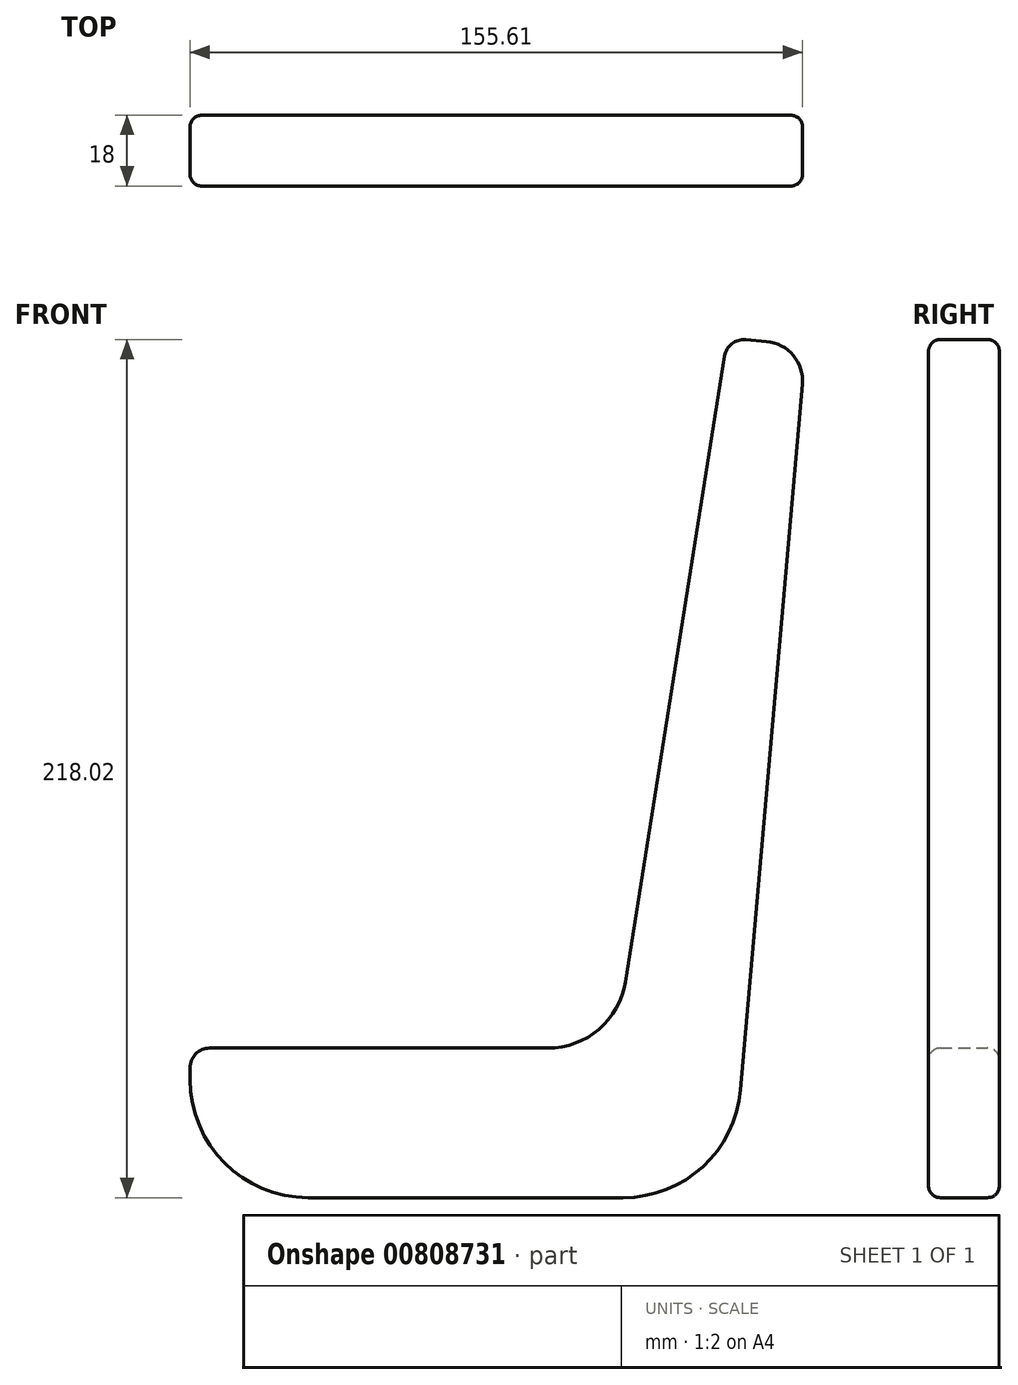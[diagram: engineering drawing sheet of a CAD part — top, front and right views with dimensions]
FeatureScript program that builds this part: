
annotation { "Feature Type Name" : "Feature", "Feature Type Description" : "" }
export const myFeature = defineFeature(function(context is Context, id is Id, definition is map)
    precondition{}
    {
        {
            var Q0;
            Q0=qCreatedBy(makeId("Front.planeOp"),FACE);
            var sketch = newSketch(context, id + "F0", { "sketchPlane" : qUnion([Q0])});
            skLineSegment(sketch, "E0", {"start": v(-17.08, 0) * mm, "end": v(-102.95, 0) * mm});
            skLineSegment(sketch, "E1", {"start": v(-107.95, -5) * mm, "end": v(-107.95, -8) * mm});
            skLineSegment(sketch, "E2", {"start": v(-77.95, -38) * mm, "end": v(2.05, -38) * mm});
            skLineSegment(sketch, "E3", {"start": v(31.94, -10.61) * mm, "end": v(47.63, 168.7) * mm});
            skLineSegment(sketch, "E4", {"start": v(38.54, 179.53) * mm, "end": v(33.22, 180) * mm});
            skLineSegment(sketch, "E5", {"start": v(27.84, 175.8) * mm, "end": v(2.67, 16.87) * mm});
            skPoint(sketch, "E6.visualSharp", {"position": v(29.54, -38) * mm});
            skArc(sketch, "E6.filletArc", {"start": v(2.05, -38) * mm, "mid": v(22.32, -30.12) * mm, "end": v(31.94, -10.61) * mm});
            skPoint(sketch, "E7.visualSharp", {"position": v(0, 0) * mm});
            skArc(sketch, "E7.filletArc", {"start": v(-17.08, 0) * mm, "mid": v(-4.1, 4.8) * mm, "end": v(2.67, 16.87) * mm});
            skPoint(sketch, "E8.visualSharp", {"position": v(-107.95, -38) * mm});
            skArc(sketch, "E8.filletArc", {"start": v(-107.95, -8) * mm, "mid": v(-99.16, -29.21) * mm, "end": v(-77.95, -38) * mm});
            skPoint(sketch, "E9.visualSharp", {"position": v(48.5, 178.66) * mm});
            skArc(sketch, "E9.filletArc", {"start": v(47.63, 168.7) * mm, "mid": v(45.32, 176) * mm, "end": v(38.54, 179.53) * mm});
            skPoint(sketch, "E10.visualSharp", {"position": v(-107.95, 0) * mm});
            skArc(sketch, "E10.filletArc", {"start": v(-102.95, 0) * mm, "mid": v(-106.48, -1.46) * mm, "end": v(-107.95, -5) * mm});
            skPoint(sketch, "E11.visualSharp", {"position": v(28.57, 180.4) * mm});
            skArc(sketch, "E11.filletArc", {"start": v(33.22, 180) * mm, "mid": v(29.7, 178.96) * mm, "end": v(27.84, 175.8) * mm});
            skLineSegment(sketch, "E12", {"start": v(-107.95, 0) * mm, "end": v(-107.95, -10) * mm, "construction": true});
            skLineSegment(sketch, "E13", {"start": v(-107.95, -10) * mm, "end": v(-57.95, -10) * mm, "construction": true});
            skPoint(sketch, "E14", {"position": v(-57.95, -10) * mm});
            skLineSegment(sketch, "E15", {"start": v(38.54, 179.53) * mm, "end": v(30.71, 130.15) * mm, "construction": true});
            skPoint(sketch, "E16", {"position": v(30.71, 130.15) * mm});
            skSolve(sketch);
        }
        {
            var Q0;
            Q0=makeQuery(id+"F0.imprint","IMPRINT",FACE,{"disambiguationData":[TD([[makeQuery(id+"F0.imprint","IMPRINT",EDGE,{"derivedFrom":sQuery(id+"F0.wireOp",EDGE,"E0")}),1.0]])]});
            extrude(context, id + "F1", {"entities" : qUnion([Q0]), "depth" : 18 * mm, "offsetDistance" : 25 * mm});
        }
        {
            var Q0;
            Q0=makeQuery(id+"F1.opExtrude","CAP_FACE",FACE,{"disambiguationData":[OSD([sQuery(id+"F0.wireOp",EDGE,"E0"),sQuery(id+"F0.wireOp",EDGE,"E1"),sQuery(id+"F0.wireOp",EDGE,"E2"),sQuery(id+"F0.wireOp",EDGE,"E3"),sQuery(id+"F0.wireOp",EDGE,"E4"),sQuery(id+"F0.wireOp",EDGE,"E5"),sQuery(id+"F0.wireOp",EDGE,"E6.filletArc"),sQuery(id+"F0.wireOp",EDGE,"E7.filletArc"),sQuery(id+"F0.wireOp",EDGE,"E8.filletArc"),sQuery(id+"F0.wireOp",EDGE,"E9.filletArc"),sQuery(id+"F0.wireOp",EDGE,"E10.filletArc"),sQuery(id+"F0.wireOp",EDGE,"E11.filletArc")])],"isStart":false});
            var sketch = newSketch(context, id + "F2", { "sketchPlane" : qUnion([Q0])});
            skPoint(sketch, "E17.0", {"position": v(30.71, 130.15) * mm});
            skPoint(sketch, "E18.0", {"position": v(-57.95, -10) * mm});
            skSolve(sketch);
        }
        {
            var Q0;
            Q0=makeQuery(id+"F1.opExtrude","CAP_FACE",FACE,{"disambiguationData":[OSD([sQuery(id+"F0.wireOp",EDGE,"E0"),sQuery(id+"F0.wireOp",EDGE,"E1"),sQuery(id+"F0.wireOp",EDGE,"E2"),sQuery(id+"F0.wireOp",EDGE,"E3"),sQuery(id+"F0.wireOp",EDGE,"E4"),sQuery(id+"F0.wireOp",EDGE,"E5"),sQuery(id+"F0.wireOp",EDGE,"E6.filletArc"),sQuery(id+"F0.wireOp",EDGE,"E7.filletArc"),sQuery(id+"F0.wireOp",EDGE,"E8.filletArc"),sQuery(id+"F0.wireOp",EDGE,"E9.filletArc"),sQuery(id+"F0.wireOp",EDGE,"E10.filletArc"),sQuery(id+"F0.wireOp",EDGE,"E11.filletArc")])],"isStart":true});
            var Q1;
            Q1=makeQuery(id+"F1.opExtrude","CAP_FACE",FACE,{"disambiguationData":[OSD([sQuery(id+"F0.wireOp",EDGE,"E0"),sQuery(id+"F0.wireOp",EDGE,"E1"),sQuery(id+"F0.wireOp",EDGE,"E2"),sQuery(id+"F0.wireOp",EDGE,"E3"),sQuery(id+"F0.wireOp",EDGE,"E4"),sQuery(id+"F0.wireOp",EDGE,"E5"),sQuery(id+"F0.wireOp",EDGE,"E6.filletArc"),sQuery(id+"F0.wireOp",EDGE,"E7.filletArc"),sQuery(id+"F0.wireOp",EDGE,"E8.filletArc"),sQuery(id+"F0.wireOp",EDGE,"E9.filletArc"),sQuery(id+"F0.wireOp",EDGE,"E10.filletArc"),sQuery(id+"F0.wireOp",EDGE,"E11.filletArc")])],"isStart":false});
            fillet(context, id + "F3", {"entities" : qUnion([Q0, Q1]), "radius" : 3 * mm, "tangentPropagation" : true, "allowEdgeOverflow" : false});
        }
    });
